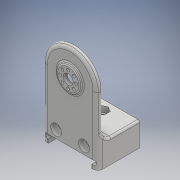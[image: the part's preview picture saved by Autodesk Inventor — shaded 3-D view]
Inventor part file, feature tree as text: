
AUTODESK INVENTOR PART (.ipt)
format: ipt  version: 2018 (Build 220112000, 112)  size: 1,486,336 bytes
history: native  units: mm
features: sketch x12, extrude x10, fillet x7, projected_geometry x6, hole x2, chamfer x1
ambient origin geometry x8: Origin, YZ Plane, XZ Plane, XY Plane, X Axis, Y Axis, Z Axis, Center Point
bodies: Solid1 (feature_tree)
feature tree (38):
  extrude  "Extrusion1"  Depth=1.0mm
  sketch  "Sketch2"  dims[d0=20.5mm d1=0.0mm d2=1.0mm]
  extrude  "Extrusion2"  Depth=56.0mm
  extrude  "Extrusion3"  Depth=44.0mm
  hole  "Hole1"  [1 undecoded]
  extrude  "Extrusion4"  Depth=14.0mm
  extrude  "Extrusion5"  Depth=31.5mm TaperAngle=0.0deg
  sketch  "Sketch6"  dims[d11=14.0mm d12=14.0mm]
  hole  "Hole2"  [1 undecoded]
  extrude  "Extrusion6"  Depth=10.0mm
  fillet  "Fillet1"  Radius=5.4mm
  sketch  "Sketch9"  dims[d24=8.0mm d25=0.0mm d26=10.0mm]
  extrude  "Extrusion7"  Depth=8.0mm
  fillet  "Fillet4"  Radius=10.0mm
  extrude  "Extrusion8"  Depth=2.9mm
  extrude  "Extrusion9"  Depth=15.0mm
  chamfer  "Chamfer1"  Distance=6.0mm
  fillet  "Fillet5"  Radius=10.0mm
  fillet  "Fillet6"  Radius=1.0mm
  fillet  "Fillet7"  Radius=18.5mm
  fillet  "Fillet8"  Radius=2.0mm
  extrude  "Extrusion10"  Depth=2.0mm TaperAngle=45.0deg
  fillet  "Fillet9"  Radius=2.0mm
  sketch  "Sketch3"  dims[d3=250.0mm d4=56.0mm]
  projected_geometry  "Projected Loop1"
  sketch  "Sketch4"  dims[d5=16.0mm d6=44.0mm]
  sketch  "Sketch5"  dims[d7=5.0mm d8=0.0mm d9=42.0mm d10=0.0mm]
  projected_geometry  "Projected Loop2"
  sketch  "Sketch7"  dims[d13=7.0mm d14=6.0mm d15=4.0mm d16=2.0mm d17=90.0deg d18=8.0mm d19=20.594885mm d20=31.5mm d21=0.0mm]
  projected_geometry  "Projected Loop3"
  sketch  "Sketch8"  dims[d22=11.0mm d23=11.0mm]
  projected_geometry  "Projected Loop4"
  sketch  "Sketch11"  dims[d27=7.0mm d28=6.0mm d29=4.0mm d30=2.0mm d31=90.0deg d32=8.0mm d33=20.594885mm d34=5.4mm]
  sketch  "Sketch13"  dims[d35=6.0mm d36=0.0mm d37=8.0mm d38=10.0mm]
  projected_geometry  "Projected Loop6"
  sketch  "Sketch14"  dims[d39=16.0mm d40=2.9mm]
  projected_geometry  "Projected Loop7"
  sketch  "Sketch15"  dims[d41=80.0mm d43=360.0deg d55=15.0mm d56=6.0mm d58=10.0mm d59=0.0mm d60=1.0mm d63=18.5mm d64=0.0mm d65=2.0mm d66=0.0mm d67=2.0mm d68=2.0mm d69=45.0deg d70=2.0mm d71=0.5mm d72=5.0mm d73=2.0mm d74=60.0mm d75=0.5mm d76=0.0mm d77=0.25mm]
note: 2 required parameter values undecoded (feature->parameter linkage not recoverable at this tier; creation-order binding heuristic only, values carry confidence <= 0.55)
